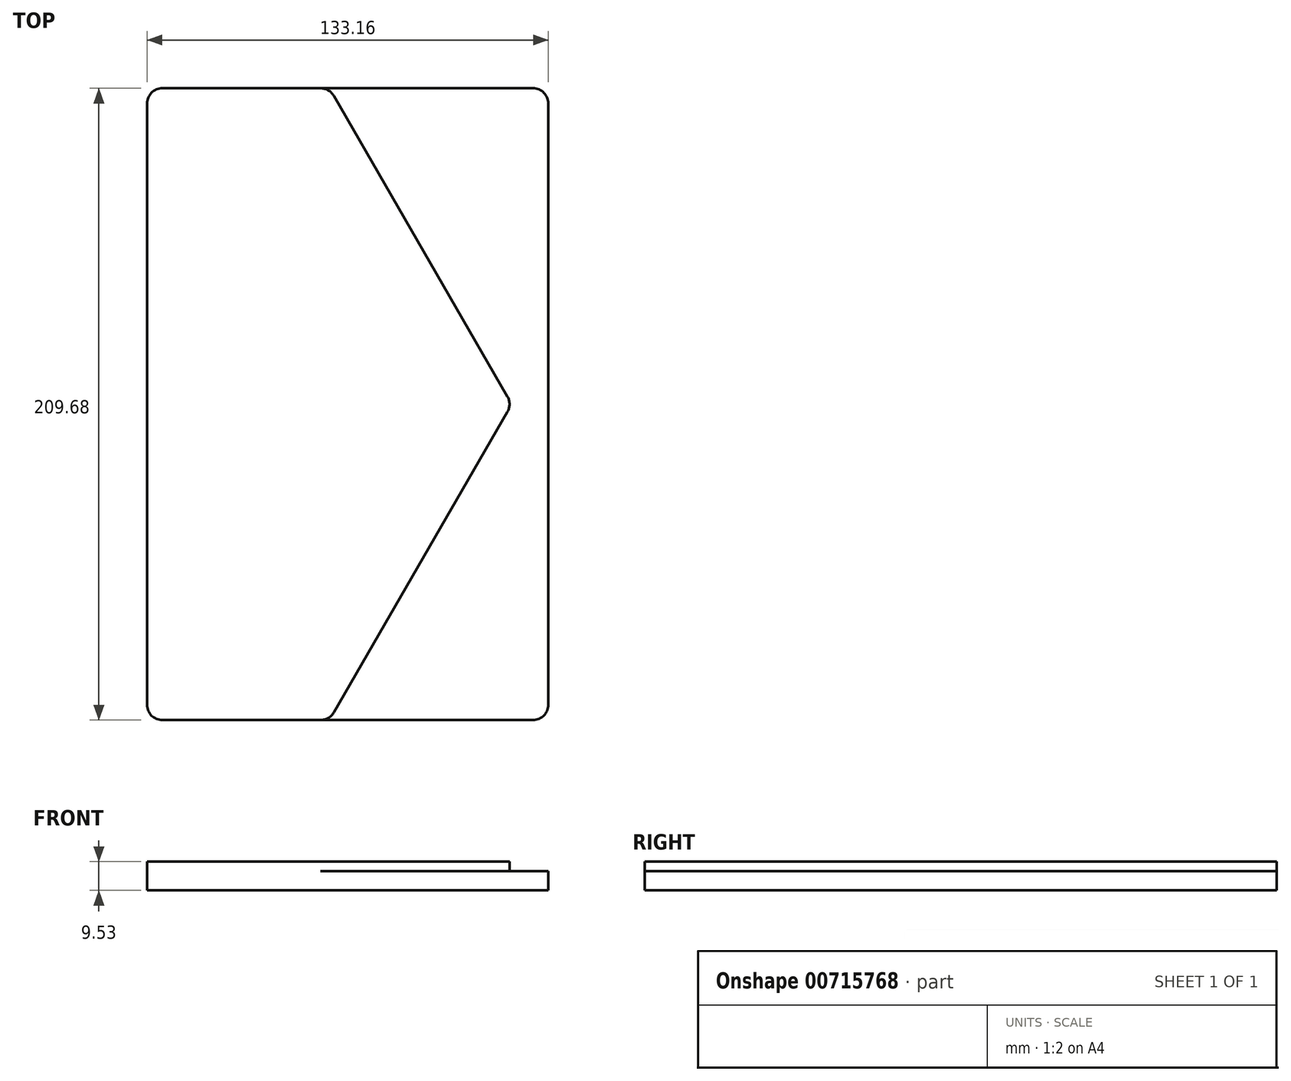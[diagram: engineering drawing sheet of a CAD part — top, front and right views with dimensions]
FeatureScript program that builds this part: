
annotation { "Feature Type Name" : "Feature", "Feature Type Description" : "" }
export const myFeature = defineFeature(function(context is Context, id is Id, definition is map)
    precondition{}
    {
        {
            var Q0;
            Q0=qCreatedBy(makeId("Top.planeOp"),FACE);
            var sketch = newSketch(context, id + "F0", { "sketchPlane" : qUnion([Q0])});
            skLineSegment(sketch, "E0.bottom", {"start": v(-66.58, -59.92) * mm, "end": v(66.58, -59.92) * mm});
            skLineSegment(sketch, "E0.top", {"start": v(-66.58, 149.76) * mm, "end": v(66.58, 149.76) * mm});
            skLineSegment(sketch, "E0.left", {"start": v(-66.58, -59.92) * mm, "end": v(-66.58, 149.76) * mm});
            skLineSegment(sketch, "E0.right", {"start": v(66.58, -59.92) * mm, "end": v(66.58, 149.76) * mm});
            skPoint(sketch, "E0.middle", {"position": v(0, 44.92) * mm});
            skSolve(sketch);
        }
        {
            var Q0;
            Q0=makeQuery(id+"F0.imprint","IMPRINT",FACE,{"disambiguationData":[TD([[makeQuery(id+"F0.imprint","IMPRINT",EDGE,{"derivedFrom":sQuery(id+"F0.wireOp",EDGE,"E0.bottom")}),1.0]])]});
            extrude(context, id + "F1", {"entities" : qUnion([Q0]), "depth" : 6.35 * mm, "offsetDistance" : 25.4 * mm});
        }
        {
            var Q0;
            Q0=makeQuery(id+"F1.opExtrude","CAP_FACE",FACE,{"disambiguationData":[OSD([sQuery(id+"F0.wireOp",EDGE,"E0.bottom"),sQuery(id+"F0.wireOp",EDGE,"E0.top"),sQuery(id+"F0.wireOp",EDGE,"E0.left"),sQuery(id+"F0.wireOp",EDGE,"E0.right")])],"isStart":false});
            var sketch = newSketch(context, id + "F2", { "sketchPlane" : qUnion([Q0])});
            skCircle(sketch, "E1.cCircle", {"center": v(-66.58, 44.92) * mm, "radius": 104.84 * mm, "construction": true});
            skLineSegment(sketch, "E1.0", {"start": v(-6.05, -59.92) * mm, "end": v(-127.1, -59.92) * mm});
            skLineSegment(sketch, "E1.1", {"start": v(-127.1, -59.92) * mm, "end": v(-187.63, 44.92) * mm});
            skLineSegment(sketch, "E1.2", {"start": v(-187.63, 44.92) * mm, "end": v(-127.1, 149.76) * mm});
            skLineSegment(sketch, "E1.3", {"start": v(-127.1, 149.76) * mm, "end": v(-6.05, 149.76) * mm});
            skLineSegment(sketch, "E1.4", {"start": v(-6.05, 149.76) * mm, "end": v(54.48, 44.92) * mm});
            skLineSegment(sketch, "E1.5", {"start": v(54.48, 44.92) * mm, "end": v(-6.05, -59.92) * mm});
            skPoint(sketch, "E1.0.midPoint", {"position": v(-66.58, -59.92) * mm});
            skSolve(sketch);
        }
        {
            var Q0;
            Q0=makeQuery(id+"F1.opExtrude","SWEPT_EDGE",EDGE,{"disambiguationData":[OSD([sQuery(id+"F0.wireOp",EDGE,"E0.bottom"),sQuery(id+"F0.wireOp",EDGE,"E0.right")])]});
            var Q1;
            {var subQ0=sQuery(id+"F0.wireOp",EDGE,"E0.left");Q1=makeQuery(id+"F4.boolean.opBoolean","MERGE",EDGE,{"derivedFrom":[makeQuery(id+"F1.opExtrude","SWEPT_EDGE",EDGE,{"disambiguationData":[OSD([sQuery(id+"F0.wireOp",EDGE,"E0.bottom"),subQ0])]}),makeQuery(id+"F4.opExtrude","SWEPT_EDGE",EDGE,{"disambiguationData":[OSD([subQ0,sQuery(id+"F2.wireOp",EDGE,"E1.0")])]})]});}
            var Q2;
            {var subQ0=sQuery(id+"F0.wireOp",EDGE,"E0.left");Q2=makeQuery(id+"F4.boolean.opBoolean","MERGE",EDGE,{"derivedFrom":[makeQuery(id+"F1.opExtrude","SWEPT_EDGE",EDGE,{"disambiguationData":[OSD([sQuery(id+"F0.wireOp",EDGE,"E0.top"),subQ0])]}),makeQuery(id+"F4.opExtrude","SWEPT_EDGE",EDGE,{"disambiguationData":[OSD([subQ0,sQuery(id+"F2.wireOp",EDGE,"E1.3")])]})]});}
            var Q3;
            Q3=makeQuery(id+"F1.opExtrude","SWEPT_EDGE",EDGE,{"disambiguationData":[OSD([sQuery(id+"F0.wireOp",EDGE,"E0.top"),sQuery(id+"F0.wireOp",EDGE,"E0.right")])]});
            fillet(context, id + "F3", {"entities" : qUnion([Q0, Q1, Q2, Q3]), "radius" : 5.08 * mm, "tangentPropagation" : true, "allowEdgeOverflow" : false});
        }
        {
            var Q0;
            {var subQ1=sQuery(id+"F2.wireOp",EDGE,"E1.4");Q0=makeQuery(id+"F2.imprint","IMPRINT",FACE,{"disambiguationData":[TD([[makeQuery(id+"F2.imprint","IMPRINT",EDGE,{"derivedFrom":subQ1}),-1.0]])]});}
            extrude(context, id + "F4", {"entities" : qUnion([Q0]), "operationType" : NewBodyOperationType.ADD, "depth" : 3.17 * mm, "offsetDistance" : 25.4 * mm});
        }
        {
            var Q0;
            {var subQ0=sQuery(id+"F2.wireOp",EDGE,"E1.5");var subQ1=sQuery(id+"F2.wireOp",EDGE,"E1.4");Q0=makeQuery(id+"FSqdfQ9FHJSbXOy_1.boolean.opBoolean","MERGE",EDGE,{"derivedFrom":[makeQuery(id+"F4.opExtrude","SWEPT_EDGE",EDGE,{"disambiguationData":[OSD([subQ1,subQ0])]}),makeQuery(id+"FSqdfQ9FHJSbXOy_1.opExtrude","SWEPT_EDGE",EDGE,{"disambiguationData":[OSD([subQ1,subQ0])]})]});}
            var Q1;
            Q1=makeQuery(id+"F4.opExtrude","SWEPT_EDGE",EDGE,{"disambiguationData":[OSD([sQuery(id+"F0.wireOp",EDGE,"E0.bottom"),sQuery(id+"F2.wireOp",EDGE,"E1.0"),sQuery(id+"F2.wireOp",EDGE,"E1.5")])]});
            var Q2;
            Q2=makeQuery(id+"F4.opExtrude","SWEPT_EDGE",EDGE,{"disambiguationData":[OSD([sQuery(id+"F0.wireOp",EDGE,"E0.top"),sQuery(id+"F2.wireOp",EDGE,"E1.3"),sQuery(id+"F2.wireOp",EDGE,"E1.4")])]});
            fillet(context, id + "F5", {"entities" : qUnion([Q0, Q1, Q2]), "radius" : 5.08 * mm, "tangentPropagation" : true, "allowEdgeOverflow" : false});
        }
        {
            var Q0;
            Q0=makeQuery(id+"F4.opExtrude","SWEPT_EDGE",EDGE,{"disambiguationData":[OSD([sQuery(id+"F0.wireOp",EDGE,"E0.left"),sQuery(id+"F2.wireOp",EDGE,"E1.0")])]});
            var Q1;
            Q1=makeQuery(id+"F4.opExtrude","SWEPT_EDGE",EDGE,{"disambiguationData":[OSD([sQuery(id+"F0.wireOp",EDGE,"E0.left"),sQuery(id+"F2.wireOp",EDGE,"E1.3")])]});
            fillet(context, id + "F6", {"entities" : qUnion([Q0, Q1]), "radius" : 5.08 * mm, "tangentPropagation" : true, "allowEdgeOverflow" : false});
        }
    });
